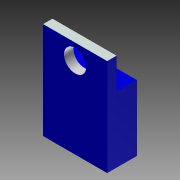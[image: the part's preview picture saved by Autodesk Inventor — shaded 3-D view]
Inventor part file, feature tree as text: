
AUTODESK INVENTOR PART (.ipt)
format: ipt  version: 2012 (Build 160160000, 160)  size: 90,624 bytes
history: native  units: in
note: dims shown in document units (in); Inventor stores cm internally (conversion verified against a paired STEP export)
features: sketch x3, extrude x2, hole x1
ambient origin geometry x8: Origin, YZ Plane, XZ Plane, XY Plane, X Axis, Y Axis, Z Axis, Center Point
bodies: Solid1 (feature_tree)
feature tree (6):
  extrude  "Extrusion1"  Depth=0.42in
  extrude  "Extrusion2"  Depth=0.2in
  hole  "Hole1"  [1 undecoded]
  sketch  "Sketch1"  dims[d0=0.41in d1=0.42in]
  sketch  "Sketch2"  dims[d2=0.19in d3=0.0in d4=0.2in]
  sketch  "Sketch3"  dims[d5=0.06in d6=0.0in d7=0.52in d8=0.142in d9=0.75in d10=0.375in d11=0.25in d12=0.5635in d13=1.0in d14=0.8108in]
note: 1 required parameter value undecoded (feature->parameter linkage not recoverable at this tier; creation-order binding heuristic only, values carry confidence <= 0.55)
